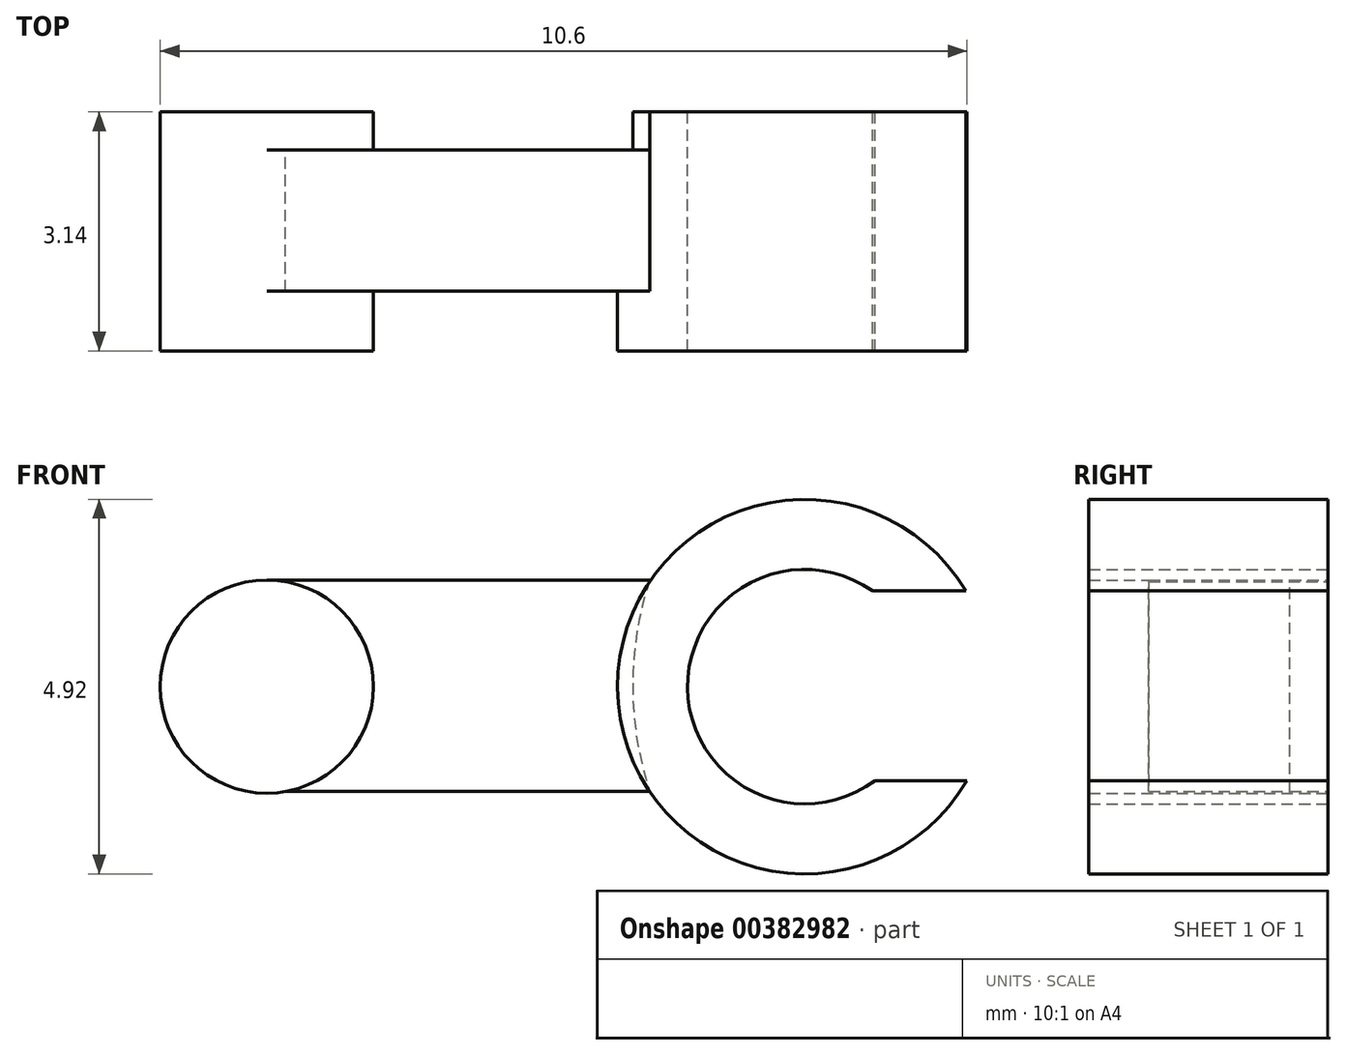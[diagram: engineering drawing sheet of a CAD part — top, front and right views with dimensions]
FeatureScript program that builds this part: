
annotation { "Feature Type Name" : "Feature", "Feature Type Description" : "" }
export const myFeature = defineFeature(function(context is Context, id is Id, definition is map)
    precondition{}
    {
        {
            var Q0;
            Q0=qCreatedBy(makeId("Front.planeOp"),FACE);
            var sketch = newSketch(context, id + "F0", { "sketchPlane" : qUnion([Q0])});
            skCircle(sketch, "E0", {"center": v(0, 0) * mm, "radius": 1.4 * mm});
            skPoint(sketch, "E1.center.orphan", {"position": v(0, 1.4) * mm});
            skArc(sketch, "E2", {"start": v(9.18, 1.26) * mm, "mid": v(4.6, -0.01) * mm, "end": v(9.2, -1.23) * mm});
            skArc(sketch, "E3", {"start": v(7.96, 1.26) * mm, "mid": v(5.53, -0.02) * mm, "end": v(7.99, -1.23) * mm});
            skLineSegment(sketch, "E4", {"start": v(7.96, 1.26) * mm, "end": v(9.18, 1.26) * mm});
            skLineSegment(sketch, "E5", {"start": v(7.99, -1.23) * mm, "end": v(9.2, -1.23) * mm});
            skPoint(sketch, "E6.start.orphan", {"position": v(0, -1.4) * mm});
            skLineSegment(sketch, "E7.bottom", {"start": v(0, 1.4) * mm, "end": v(5.03, 1.4) * mm});
            skLineSegment(sketch, "E7.top", {"start": v(0, -1.38) * mm, "end": v(5.03, -1.38) * mm});
            skLineSegment(sketch, "E7.right", {"start": v(5.03, 1.4) * mm, "end": v(5.03, 1.38) * mm});
            skSolve(sketch);
        }
        {
            var Q0;
            {var subQ5=sQuery(id+"F0.wireOp",EDGE,"E7.bottom");Q0=makeQuery(id+"F0.imprint","IMPRINT",FACE,{"disambiguationData":[TD([[makeQuery(id+"F0.imprint","IMPRINT",EDGE,{"derivedFrom":subQ5}),-1.0]])]});}
            extrude(context, id + "F1", {"entities" : qUnion([Q0]), "depth" : 1.57 * mm, "offsetDistance" : 25 * mm});
        }
        {
            var Q0;
            Q0=makeQuery(id+"F0.imprint","IMPRINT",FACE,{"disambiguationData":[TD([[makeQuery(id+"F0.imprint","IMPRINT",EDGE,{"derivedFrom":sQuery(id+"F0.wireOp",EDGE,"E3")}),-1.0]])]});
            extrude(context, id + "F2", {"entities" : qUnion([Q0]), "operationType" : NewBodyOperationType.ADD, "depth" : 3.14 * mm, "offsetDistance" : 25 * mm});
        }
        {
            var Q0;
            {var subQ0=sQuery(id+"F0.wireOp",EDGE,"E2");Q0=makeQuery(id+"F2.boolean.opBoolean","MERGE",FACE,{"derivedFrom":[makeQuery(id+"F1.opExtrude","CAP_FACE",FACE,{"disambiguationData":[OSD([sQuery(id+"F0.wireOp",EDGE,"E0"),subQ0,sQuery(id+"F0.wireOp",EDGE,"E7.bottom"),sQuery(id+"F0.wireOp",EDGE,"E7.top"),sQuery(id+"F0.wireOp",EDGE,"E7.right")])],"isStart":true}),makeQuery(id+"F2.opExtrude","CAP_FACE",FACE,{"disambiguationData":[OSD([subQ0,sQuery(id+"F0.wireOp",EDGE,"E3"),sQuery(id+"F0.wireOp",EDGE,"E4"),sQuery(id+"F0.wireOp",EDGE,"E5")])],"isStart":true})]});}
            var sketch = newSketch(context, id + "F3", { "sketchPlane" : qUnion([Q0])});
            skArc(sketch, "E8", {"start": v(-5.03, -1.38) * mm, "mid": v(-4.8, 0.01) * mm, "end": v(-5.03, 1.4) * mm});
            skSolve(sketch);
        }
        {
            var Q0;
            Q0=qSketchRegion(id+"F3",true);
            var Q1;
            Q1=makeQuery(id+"F3.imprint","IMPRINT",FACE,{"disambiguationData":[TD([[makeQuery(id+"F3.imprint","IMPRINT",EDGE,{"derivedFrom":sQuery(id+"F3.wireOp",EDGE,"E8")}),-1.0]])]});
            extrude(context, id + "F4", {"entities" : qUnion([Q0, Q1]), "operationType" : NewBodyOperationType.REMOVE, "oppositeDirection" : true, "depth" : .5 * mm, "offsetDistance" : 25 * mm});
        }
        {
            var Q0;
            {var subQ0=sQuery(id+"F0.wireOp",EDGE,"E0");var subQ1=makeQuery(id+"F0.imprint","INTERSECT",VERTEX,{"derivedFrom":[subQ0,sQuery(id+"F0.wireOp",EDGE,"E7.bottom")]});Q0=makeQuery(id+"F0.imprint","IMPRINT",FACE,{"disambiguationData":[TD([[makeQuery(id+"F0.imprint","IMPRINT",EDGE,{"disambiguationData":[TD([[subQ1,-1.0]])],"derivedFrom":subQ0}),1.0]])]});}
            extrude(context, id + "F5", {"entities" : qUnion([Q0]), "operationType" : NewBodyOperationType.ADD, "depth" : 3.14 * mm, "offsetDistance" : 25 * mm});
        }
        {
            var Q0;
            Q0=makeQuery(id+"F1.opExtrude","CAP_FACE",FACE,{"disambiguationData":[OSD([sQuery(id+"F0.wireOp",EDGE,"E0"),sQuery(id+"F0.wireOp",EDGE,"E2"),sQuery(id+"F0.wireOp",EDGE,"E7.bottom"),sQuery(id+"F0.wireOp",EDGE,"E7.top"),sQuery(id+"F0.wireOp",EDGE,"E7.right")])],"isStart":false});
            extrude(context, id + "F6", {"entities" : qUnion([Q0]), "operationType" : NewBodyOperationType.ADD, "depth" : .785 * mm, "offsetDistance" : 25 * mm});
        }
    });
